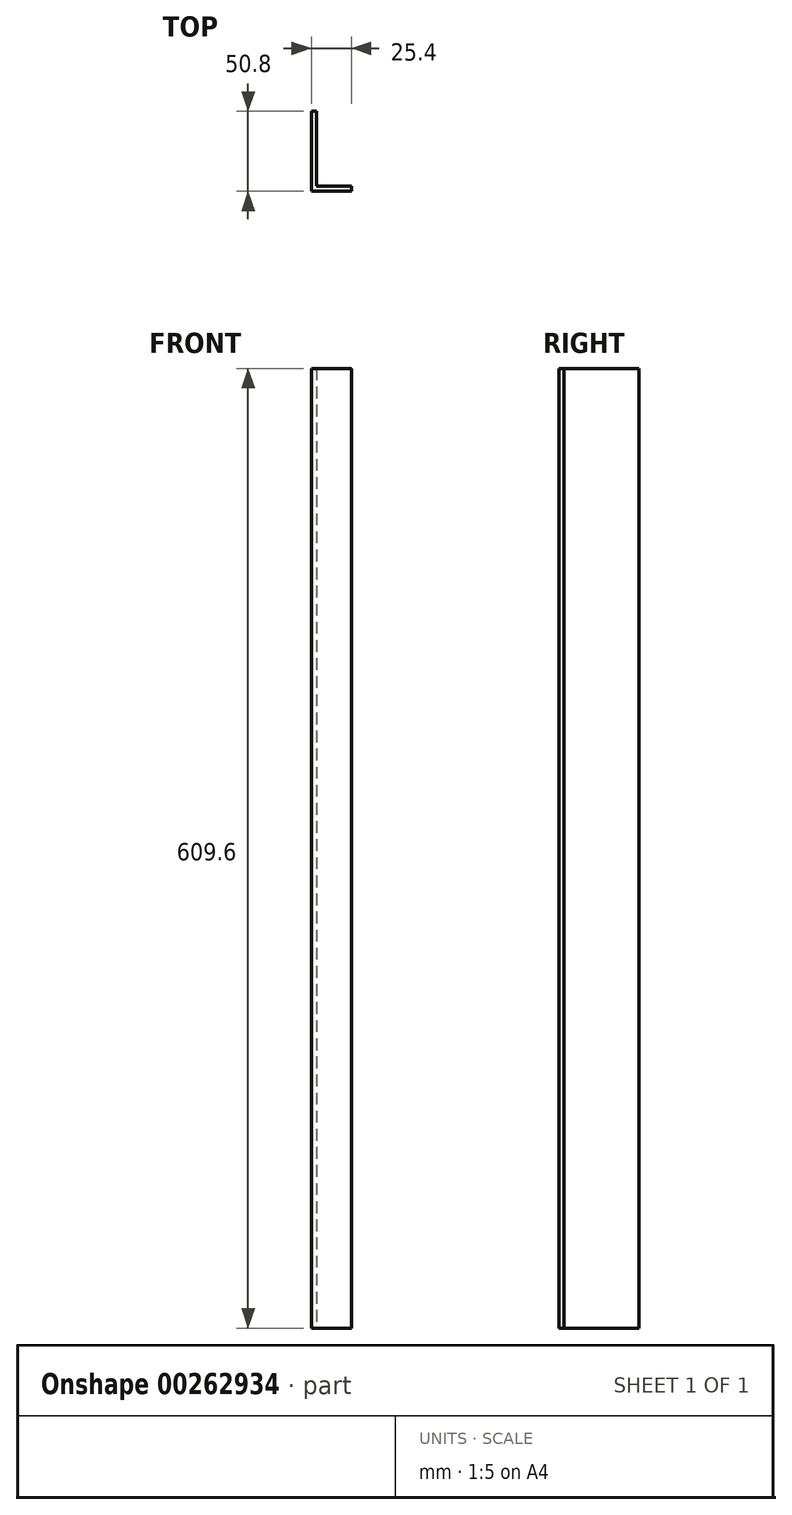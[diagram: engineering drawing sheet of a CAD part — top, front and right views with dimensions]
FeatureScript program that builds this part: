
annotation { "Feature Type Name" : "Feature", "Feature Type Description" : "" }
export const myFeature = defineFeature(function(context is Context, id is Id, definition is map)
    precondition{}
    {
        {
            var Q0;
            Q0=qCreatedBy(makeId("Top.planeOp"),FACE);
            var sketch = newSketch(context, id + "F0", { "sketchPlane" : qUnion([Q0])});
            skLineSegment(sketch, "E0", {"start": v(0, 0) * mm, "end": v(25.4, 0) * mm});
            skLineSegment(sketch, "E1", {"start": v(25.4, 0) * mm, "end": v(25.4, 3.18) * mm});
            skLineSegment(sketch, "E2", {"start": v(25.4, 3.18) * mm, "end": v(3.18, 3.17) * mm});
            skLineSegment(sketch, "E3", {"start": v(3.18, 3.18) * mm, "end": v(3.18, 50.8) * mm});
            skLineSegment(sketch, "E4", {"start": v(3.18, 50.8) * mm, "end": v(0, 50.8) * mm});
            skLineSegment(sketch, "E5", {"start": v(0, 50.8) * mm, "end": v(0, 0) * mm});
            skSolve(sketch);
        }
        {
            var Q0;
            Q0 = qSketchRegion(id + "F0", true);
            extrude(context, id + "F1", {"entities" : qUnion([Q0]), "depth" : 609.6 * mm});
        }
    });
